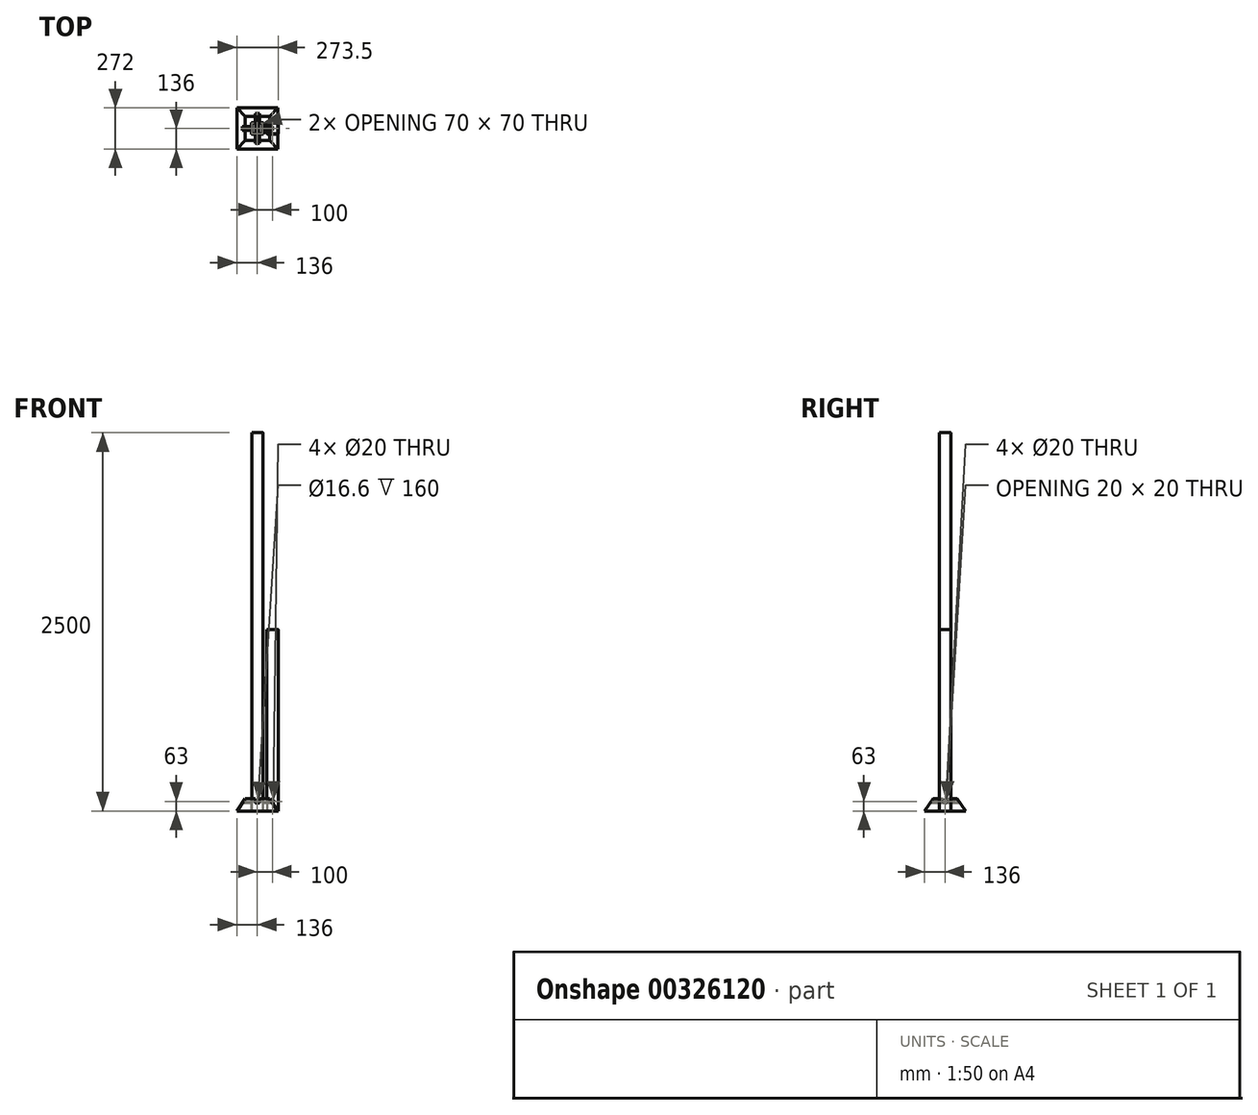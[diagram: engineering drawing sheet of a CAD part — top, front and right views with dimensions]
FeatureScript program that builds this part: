
annotation { "Feature Type Name" : "Feature", "Feature Type Description" : "" }
export const myFeature = defineFeature(function(context is Context, id is Id, definition is map)
    precondition{}
    {
        {
            var Q0;
            Q0=qCreatedBy(makeId("Top.planeOp"),FACE);
            var sketch = newSketch(context, id + "F0", { "sketchPlane" : qUnion([Q0])});
            skPoint(sketch, "E0.middle", {"position": v(0, 0) * mm});
            skLineSegment(sketch, "E1.bottom", {"start": v(-80, 80) * mm, "end": v(80, 80) * mm});
            skLineSegment(sketch, "E1.top", {"start": v(-80, -80) * mm, "end": v(80, -80) * mm});
            skLineSegment(sketch, "E1.left", {"start": v(-80, 80) * mm, "end": v(-80, -80) * mm});
            skLineSegment(sketch, "E1.right", {"start": v(80, 80) * mm, "end": v(80, -80) * mm});
            skSolve(sketch);
        }
        {
            var Q0;
            Q0=qCreatedBy(makeId("Right.planeOp"),FACE);
            var sketch = newSketch(context, id + "F1", { "sketchPlane" : qUnion([Q0])});
            skLineSegment(sketch, "E2", {"start": v(0, 0) * mm, "end": v(0, -80) * mm});
            skSolve(sketch);
        }
        {
            var Q0;
            Q0=sQuery(id+"F1.wireOp",EDGE,"E2");
            var Q1;
            Q1=sQuery(id+"F1.wireOp",VERTEX,"E2.end");
            cPlane(context, id + "F2", {"entities" : qUnion([Q0, Q1]), "cplaneType" : CPlaneType.LINE_POINT, "offset" : 25 * mm, "width" : 150 * mm, "height" : 150 * mm});
        }
        {
            var Q0;
            Q0=qCreatedBy(id+"F2.planeOp",FACE);
            var sketch = newSketch(context, id + "F3", { "sketchPlane" : qUnion([Q0])});
            skLineSegment(sketch, "E3.bottom", {"start": v(-136, 136) * mm, "end": v(136, 136) * mm});
            skLineSegment(sketch, "E3.top", {"start": v(-136, -136) * mm, "end": v(136, -136) * mm});
            skLineSegment(sketch, "E3.left", {"start": v(-136, 136) * mm, "end": v(-136, -136) * mm});
            skLineSegment(sketch, "E3.right", {"start": v(136, 136) * mm, "end": v(136, -136) * mm});
            skPoint(sketch, "E3.middle", {"position": v(0, 0) * mm});
            skSolve(sketch);
        }
        {
            var Q0;
            Q0=makeQuery(id+"F0.imprint","IMPRINT",FACE,{"disambiguationData":[TD([[makeQuery(id+"F0.imprint","IMPRINT",EDGE,{"derivedFrom":sQuery(id+"F0.wireOp",EDGE,"E1.bottom")}),-1.0]])]});
            var Q1;
            Q1=makeQuery(id+"F3.imprint","IMPRINT",FACE,{"disambiguationData":[TD([[makeQuery(id+"F3.imprint","IMPRINT",EDGE,{"derivedFrom":sQuery(id+"F3.wireOp",EDGE,"E3.bottom")}),-1.0]])]});
            loft(context, id + "F4", {"sheetProfilesArray" : [{ "sheetProfileEntities" : qUnion([Q0]) }, { "sheetProfileEntities" : qUnion([Q1]) }]});
        }
        {
            var Q0;
            Q0=makeQuery(id+"F4.opLoft","CAP_FACE",FACE,{"disambiguationData":[OSD([makeQuery(id+"F0.imprint","IMPRINT",FACE,{"disambiguationData":[TD([[makeQuery(id+"F0.imprint","IMPRINT",EDGE,{"derivedFrom":sQuery(id+"F0.wireOp",EDGE,"E1.bottom")}),-1.0]])]})])],"isStart":true});
            var sketch = newSketch(context, id + "F5", { "sketchPlane" : qUnion([Q0])});
            skLineSegment(sketch, "E4.bottom", {"start": v(-39, 39) * mm, "end": v(39, 39) * mm});
            skLineSegment(sketch, "E4.top", {"start": v(-39, -39) * mm, "end": v(39, -39) * mm});
            skLineSegment(sketch, "E4.left", {"start": v(-39, 39) * mm, "end": v(-39, -39) * mm});
            skLineSegment(sketch, "E4.right", {"start": v(39, 39) * mm, "end": v(39, -39) * mm});
            skPoint(sketch, "E4.middle", {"position": v(0, 0) * mm});
            skSolve(sketch);
        }
        {
            var Q0;
            Q0=makeQuery(id+"F5.imprint","IMPRINT",FACE,{"disambiguationData":[TD([[makeQuery(id+"F5.imprint","IMPRINT",EDGE,{"derivedFrom":sQuery(id+"F5.wireOp",EDGE,"E4.bottom")}),-1.0]])]});
            extrude(context, id + "F6", {"entities" : qUnion([Q0]), "operationType" : NewBodyOperationType.REMOVE, "endBound" : BoundingType.THROUGH_ALL, "oppositeDirection" : true, "depth" : 25 * mm});
        }
        {
            var Q0;
            Q0=qCreatedBy(makeId("Front.planeOp"),FACE);
            var sketch = newSketch(context, id + "F7", { "sketchPlane" : qUnion([Q0])});
            skLineSegment(sketch, "E5.bottom", {"start": v(-13.5, 27) * mm, "end": v(13.5, 27) * mm});
            skLineSegment(sketch, "E5.top", {"start": v(-13.5, -27) * mm, "end": v(13.5, -27) * mm});
            skLineSegment(sketch, "E5.left", {"start": v(-13.5, 27) * mm, "end": v(-13.5, -27) * mm});
            skLineSegment(sketch, "E5.right", {"start": v(13.5, 27) * mm, "end": v(13.5, -27) * mm});
            skPoint(sketch, "E5.middle", {"position": v(0, 0) * mm});
            skSolve(sketch);
        }
        {
            var Q0;
            Q0 = qSketchRegion(id + "F7", true);
            extrude(context, id + "F8", {"entities" : qUnion([Q0]), "operationType" : NewBodyOperationType.REMOVE, "endBound" : BoundingType.SYMMETRIC, "depth" : 238.2 * mm});
        }
        {
            var Q0;
            Q0=qCreatedBy(makeId("Right.planeOp"),FACE);
            var sketch = newSketch(context, id + "F9", { "sketchPlane" : qUnion([Q0])});
            skLineSegment(sketch, "E6.bottom", {"start": v(13.5, 27) * mm, "end": v(-13.5, 27) * mm});
            skLineSegment(sketch, "E6.top", {"start": v(13.5, -27) * mm, "end": v(-13.5, -27) * mm});
            skLineSegment(sketch, "E6.left", {"start": v(13.5, 27) * mm, "end": v(13.5, -27) * mm});
            skLineSegment(sketch, "E6.right", {"start": v(-13.5, 27) * mm, "end": v(-13.5, -27) * mm});
            skPoint(sketch, "E6.middle", {"position": v(0, 0) * mm});
            skSolve(sketch);
        }
        {
            var Q0;
            Q0 = qSketchRegion(id + "F9", true);
            extrude(context, id + "F10", {"entities" : qUnion([Q0]), "operationType" : NewBodyOperationType.REMOVE, "endBound" : BoundingType.SYMMETRIC, "oppositeDirection" : true, "depth" : 800 * mm});
        }
        {
            var Q0;
            Q0=qCreatedBy(id+"F2.planeOp",FACE);
            var sketch = newSketch(context, id + "F11", { "sketchPlane" : qUnion([Q0])});
            skLineSegment(sketch, "E7.bottom", {"start": v(-32.5, 37.5) * mm, "end": v(32.5, 37.5) * mm});
            skLineSegment(sketch, "E7.top", {"start": v(-32.5, -37.5) * mm, "end": v(32.5, -37.5) * mm});
            skLineSegment(sketch, "E7.left", {"start": v(-37.5, 32.5) * mm, "end": v(-37.5, -32.5) * mm});
            skLineSegment(sketch, "E7.right", {"start": v(37.5, 32.5) * mm, "end": v(37.5, -32.5) * mm});
            skPoint(sketch, "E7.middle", {"position": v(0, 0) * mm});
            skPoint(sketch, "E8.visualSharp", {"position": v(-37.5, 37.5) * mm});
            skArc(sketch, "E8.filletArc", {"start": v(-32.5, 37.5) * mm, "mid": v(-36.04, 36.04) * mm, "end": v(-37.5, 32.5) * mm});
            skPoint(sketch, "E9.visualSharp", {"position": v(37.5, 37.5) * mm});
            skArc(sketch, "E9.filletArc", {"start": v(37.5, 32.5) * mm, "mid": v(36.04, 36.04) * mm, "end": v(32.5, 37.5) * mm});
            skPoint(sketch, "E10.visualSharp", {"position": v(37.5, -37.5) * mm});
            skArc(sketch, "E10.filletArc", {"start": v(32.5, -37.5) * mm, "mid": v(36.04, -36.04) * mm, "end": v(37.5, -32.5) * mm});
            skPoint(sketch, "E11.visualSharp", {"position": v(-37.5, -37.5) * mm});
            skArc(sketch, "E11.filletArc", {"start": v(-37.5, -32.5) * mm, "mid": v(-36.04, -36.04) * mm, "end": v(-32.5, -37.5) * mm});
            skArc(sketch, "E12.0", {"start": v(-32.5, 35) * mm, "mid": v(-34.27, 34.27) * mm, "end": v(-35, 32.5) * mm});
            skLineSegment(sketch, "E12.1", {"start": v(-35, 32.5) * mm, "end": v(-35, -32.5) * mm});
            skLineSegment(sketch, "E12.2", {"start": v(-32.5, 35) * mm, "end": v(32.5, 35) * mm});
            skArc(sketch, "E12.3", {"start": v(-35, -32.5) * mm, "mid": v(-34.27, -34.27) * mm, "end": v(-32.5, -35) * mm});
            skArc(sketch, "E12.4", {"start": v(35, 32.5) * mm, "mid": v(34.27, 34.27) * mm, "end": v(32.5, 35) * mm});
            skLineSegment(sketch, "E12.5", {"start": v(35, 32.5) * mm, "end": v(35, -32.5) * mm});
            skArc(sketch, "E12.6", {"start": v(32.5, -35) * mm, "mid": v(34.27, -34.27) * mm, "end": v(35, -32.5) * mm});
            skLineSegment(sketch, "E12.7", {"start": v(-32.5, -35) * mm, "end": v(32.5, -35) * mm});
            skSolve(sketch);
        }
        {
            var Q0;
            Q0 = qSketchRegion(id + "F11", true);
            extrude(context, id + "F12", {"entities" : qUnion([Q0]), "oppositeDirection" : true, "depth" : 2500 * mm});
        }
        {
            var Q0;
            Q0=makeQuery(id+"F12.opExtrude","SWEPT_FACE",FACE,{"disambiguationData":[OSD([sQuery(id+"F11.wireOp",EDGE,"E7.bottom")])]});
            var sketch = newSketch(context, id + "F13", { "sketchPlane" : qUnion([Q0])});
            skLineSegment(sketch, "E13.0", {"start": v(13.5, -27) * mm, "end": v(-13.5, -27) * mm});
            skLineSegment(sketch, "E14", {"start": v(0, -27) * mm, "end": v(0, -17) * mm});
            skPoint(sketch, "E14.endSnap0", {"position": v(0, -27) * mm});
            skCircle(sketch, "E15", {"center": v(0, -17) * mm, "radius": 10 * mm});
            skSolve(sketch);
        }
        {
            var Q0;
            Q0=makeQuery(id+"F13.imprint","IMPRINT",FACE,{"disambiguationData":[TD([[makeQuery(id+"F13.imprint","IMPRINT",EDGE,{"derivedFrom":sQuery(id+"F13.wireOp",EDGE,"E15")}),1.0]])]});
            extrude(context, id + "F14", {"entities" : qUnion([Q0]), "operationType" : NewBodyOperationType.REMOVE, "endBound" : BoundingType.THROUGH_ALL, "oppositeDirection" : true, "depth" : 25 * mm});
        }
        {
            var Q0;
            Q0=makeQuery(id+"F12.opExtrude","SWEPT_FACE",FACE,{"disambiguationData":[OSD([sQuery(id+"F11.wireOp",EDGE,"E7.right")])]});
            var sketch = newSketch(context, id + "F15", { "sketchPlane" : qUnion([Q0])});
            skLineSegment(sketch, "E16.0", {"start": v(13.5, -27) * mm, "end": v(-13.5, -27) * mm});
            skLineSegment(sketch, "E17", {"start": v(0, -27) * mm, "end": v(0, -17) * mm});
            skPoint(sketch, "E17.endSnap0", {"position": v(0, -27) * mm});
            skCircle(sketch, "E18", {"center": v(0, -17) * mm, "radius": 10 * mm});
            skSolve(sketch);
        }
        {
            var Q0;
            Q0=makeQuery(id+"F15.imprint","IMPRINT",FACE,{"disambiguationData":[TD([[makeQuery(id+"F15.imprint","IMPRINT",EDGE,{"derivedFrom":sQuery(id+"F15.wireOp",EDGE,"E18")}),1.0]])]});
            extrude(context, id + "F16", {"entities" : qUnion([Q0]), "operationType" : NewBodyOperationType.REMOVE, "endBound" : BoundingType.THROUGH_ALL, "oppositeDirection" : true, "depth" : 25 * mm});
        }
        {
            var Q0;
            Q0=qCreatedBy(makeId("Front.planeOp"),FACE);
            var sketch = newSketch(context, id + "F17", { "sketchPlane" : qUnion([Q0])});
            skCircle(sketch, "E19.0", {"center": v(0, -17) * mm, "radius": 10 * mm});
            skCircle(sketch, "E20", {"center": v(0, -17) * mm, "radius": 9.5 * mm});
            skCircle(sketch, "E21", {"center": v(0, -17) * mm, "radius": 8.3 * mm});
            skSolve(sketch);
        }
        {
            var Q0;
            Q0=makeQuery(id+"F17.imprint","IMPRINT",FACE,{"disambiguationData":[TD([[makeQuery(id+"F17.imprint","IMPRINT",EDGE,{"derivedFrom":sQuery(id+"F17.wireOp",EDGE,"E20")}),1.0]])]});
            extrude(context, id + "F18", {"entities" : qUnion([Q0]), "endBound" : BoundingType.SYMMETRIC, "depth" : 160 * mm});
        }
        {
            var Q0;
            Q0=makeQuery(id+"F12.opExtrude","SWEPT_BODY",BODY,{"disambiguationData":[OSD([sQuery(id+"F11.wireOp",EDGE,"E7.bottom"),sQuery(id+"F11.wireOp",EDGE,"E7.top"),sQuery(id+"F11.wireOp",EDGE,"E7.left"),sQuery(id+"F11.wireOp",EDGE,"E7.right"),sQuery(id+"F11.wireOp",EDGE,"E8.filletArc"),sQuery(id+"F11.wireOp",EDGE,"E9.filletArc"),sQuery(id+"F11.wireOp",EDGE,"E10.filletArc"),sQuery(id+"F11.wireOp",EDGE,"E11.filletArc"),sQuery(id+"F11.wireOp",EDGE,"E12.0"),sQuery(id+"F11.wireOp",EDGE,"E12.1"),sQuery(id+"F11.wireOp",EDGE,"E12.2"),sQuery(id+"F11.wireOp",EDGE,"E12.3"),sQuery(id+"F11.wireOp",EDGE,"E12.4"),sQuery(id+"F11.wireOp",EDGE,"E12.5"),sQuery(id+"F11.wireOp",EDGE,"E12.6"),sQuery(id+"F11.wireOp",EDGE,"E12.7")])]});
            transform(context, id + "F19", {"entities" : qUnion([Q0]), "transformType" : TransformType.TRANSLATION_3D, "dx" : 100 * mm, "dy" : 0 * mm, "dz" : 0 * mm, "makeCopy" : true});
        }
        {
            var Q0;
            Q0=makeQuery(id+"F19.opPattern","COPY",FACE,{"derivedFrom":makeQuery(id+"F12.opExtrude","CAP_FACE",FACE,{"disambiguationData":[OSD([sQuery(id+"F11.wireOp",EDGE,"E7.bottom"),sQuery(id+"F11.wireOp",EDGE,"E7.top"),sQuery(id+"F11.wireOp",EDGE,"E7.left"),sQuery(id+"F11.wireOp",EDGE,"E7.right"),sQuery(id+"F11.wireOp",EDGE,"E8.filletArc"),sQuery(id+"F11.wireOp",EDGE,"E9.filletArc"),sQuery(id+"F11.wireOp",EDGE,"E10.filletArc"),sQuery(id+"F11.wireOp",EDGE,"E11.filletArc"),sQuery(id+"F11.wireOp",EDGE,"E12.0"),sQuery(id+"F11.wireOp",EDGE,"E12.1"),sQuery(id+"F11.wireOp",EDGE,"E12.2"),sQuery(id+"F11.wireOp",EDGE,"E12.3"),sQuery(id+"F11.wireOp",EDGE,"E12.4"),sQuery(id+"F11.wireOp",EDGE,"E12.5"),sQuery(id+"F11.wireOp",EDGE,"E12.6"),sQuery(id+"F11.wireOp",EDGE,"E12.7")])],"isStart":false}),"instanceName":"1"});
            extrude(context, id + "F20", {"entities" : qUnion([Q0]), "operationType" : NewBodyOperationType.REMOVE, "oppositeDirection" : true, "depth" : 1300 * mm});
        }
    });
